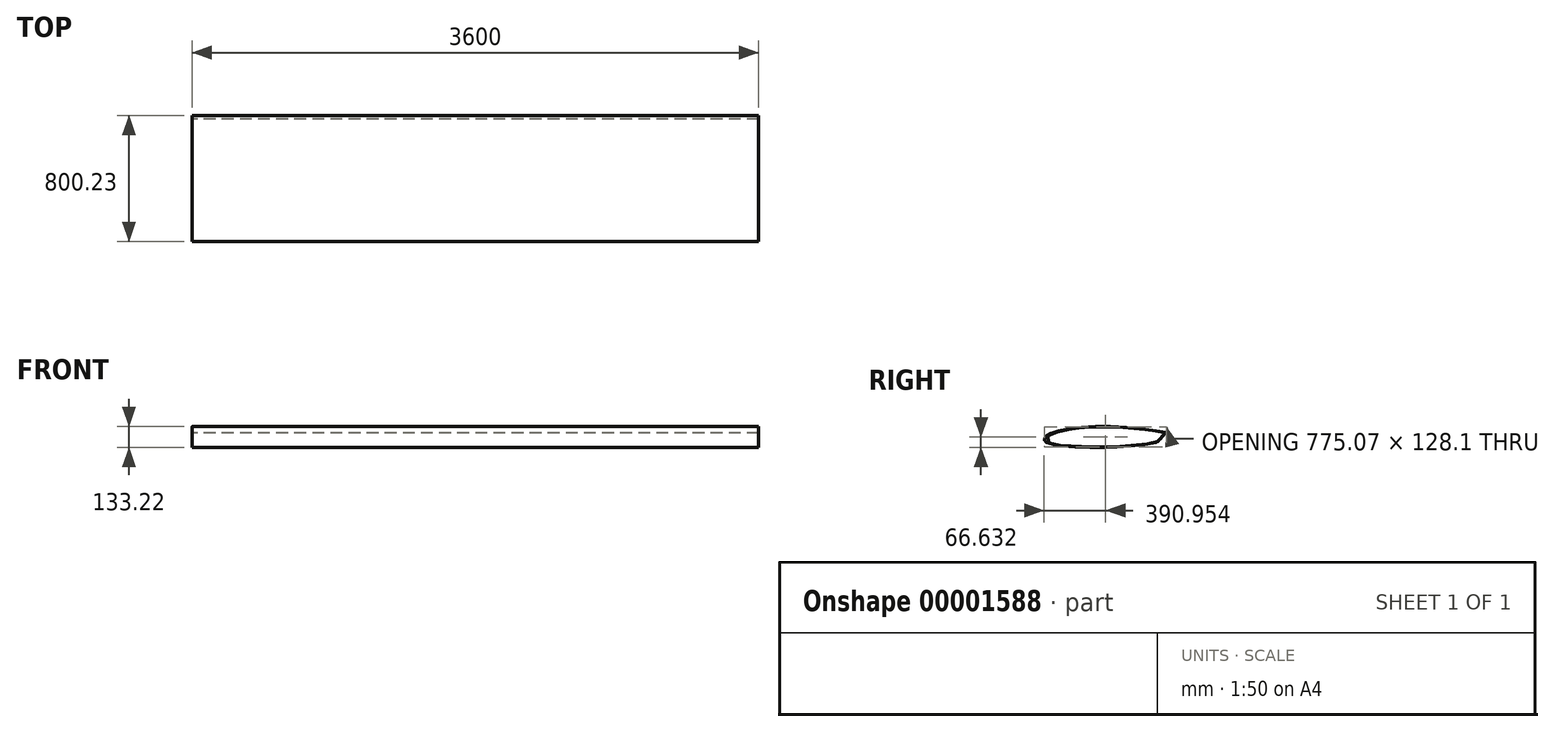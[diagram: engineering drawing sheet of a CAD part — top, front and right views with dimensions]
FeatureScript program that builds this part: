
annotation { "Feature Type Name" : "Feature", "Feature Type Description" : "" }
export const myFeature = defineFeature(function(context is Context, id is Id, definition is map)
    precondition{}
    {
        {
            var Q0;
            Q0=qCreatedBy(makeId("Right.planeOp"),FACE);
            var sketch = newSketch(context, id + "F0", { "sketchPlane" : qUnion([Q0])});
            skFitSpline(sketch, "E0", {"points": [v(383.53, 27.34) * mm, v(181.4, 54.9) * mm, v(-64.05, 68.03) * mm, v(-245.19, 53.6) * mm, v(-350.2, 31.28) * mm, v(-392.2, 14.22) * mm, v(-411.88, -1.53) * mm, v(-416.47, -11.38) * mm, v(-415.57, -19.77) * mm, v(-405.81, -29.91) * mm, v(-358.2, -47.47) * mm, v(-255.58, -59.18) * mm, v(-42.36, -65.1) * mm, v(116.33, -58.11) * mm, v(292.92, -34.26) * mm, v(321.16, -14.66) * mm, v(350.44, 24.74) * mm], "startDerivative": vector(-1979.32, 303.45) * mm, "endDerivative": vector(736.31, 60.39) * mm});
            skLineSegment(sketch, "E1", {"start": v(350.44, 24.74) * mm, "end": v(383.53, 27.34) * mm});
            skSolve(sketch);
        }
        {
            var Q0;
            Q0=makeQuery(id+"F0.imprint","IMPRINT",FACE,{"disambiguationData":[TD([[makeQuery(id+"F0.imprint","IMPRINT",EDGE,{"derivedFrom":sQuery(id+"F0.wireOp",EDGE,"E0")}),1.0]])]});
            extrude(context, id + "F1", {"entities" : qUnion([Q0]), "depth" : 3600 * mm});
        }
        {
            var Q0;
            Q0=makeQuery(id+"F1.opExtrude","CAP_FACE",FACE,{"disambiguationData":[OSD([sQuery(id+"F0.wireOp",EDGE,"E0"),sQuery(id+"F0.wireOp",EDGE,"E1")])],"isStart":true});
            var Q1;
            Q1=makeQuery(id+"F1.opExtrude","CAP_FACE",FACE,{"disambiguationData":[OSD([sQuery(id+"F0.wireOp",EDGE,"E0"),sQuery(id+"F0.wireOp",EDGE,"E1")])],"isStart":false});
            shell(context, id + "F2", {"entities" : qUnion([Q0, Q1]), "thickness" : 2.5 * mm});
        }
    });
